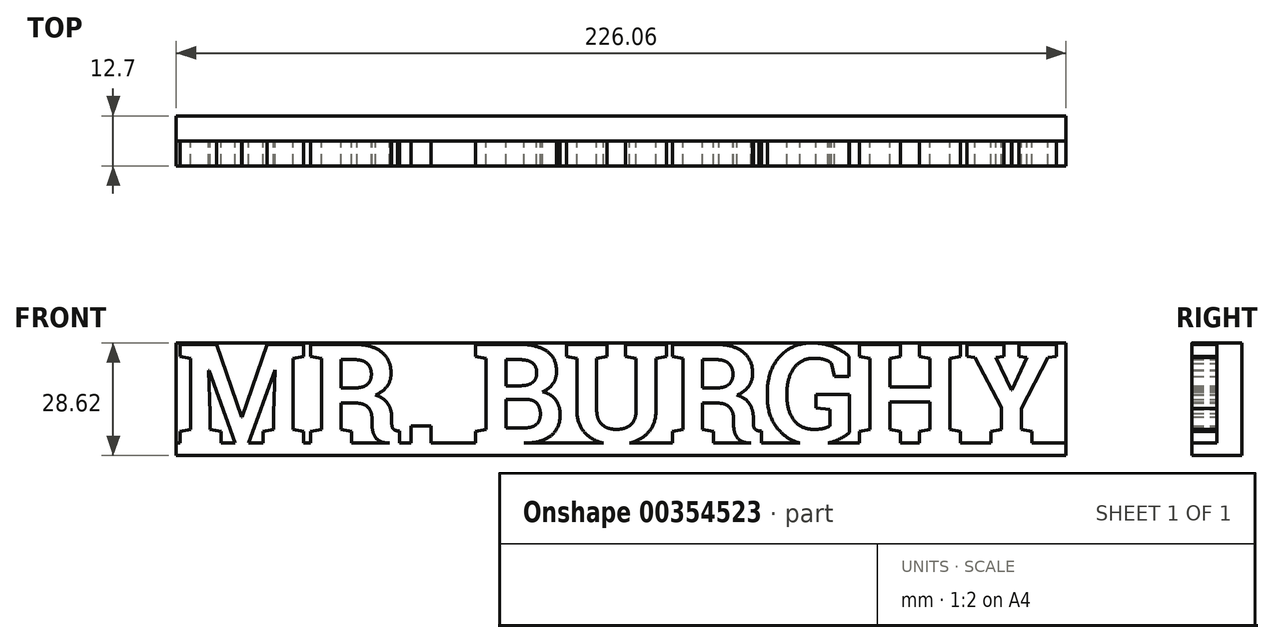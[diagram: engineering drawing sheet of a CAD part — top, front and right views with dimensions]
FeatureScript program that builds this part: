
annotation { "Feature Type Name" : "Feature", "Feature Type Description" : "" }
export const myFeature = defineFeature(function(context is Context, id is Id, definition is map)
    precondition{}
    {
        {
            var Q0;
            Q0=qCreatedBy(makeId("Front.planeOp"),FACE);
            var sketch = newSketch(context, id + "F0", { "sketchPlane" : qUnion([Q0])});
            skLineSegment(sketch, "E0.bottom", {"start": v(113.03, 0) * mm, "end": v(-113.03, 0) * mm});
            skLineSegment(sketch, "E0.top", {"start": v(113.03, 25.4) * mm, "end": v(-113.03, 25.4) * mm});
            skLineSegment(sketch, "E0.left", {"start": v(113.03, 0) * mm, "end": v(113.03, 25.4) * mm});
            skLineSegment(sketch, "E0.right", {"start": v(-113.03, 0) * mm, "end": v(-113.03, 25.4) * mm});
            skPoint(sketch, "E0.middle", {"position": v(0, 12.7) * mm});
            skSolve(sketch);
        }
        {
            var Q0;
            Q0 = qSketchRegion(id + "F0", true);
            extrude(context, id + "F1", {"entities" : qUnion([Q0]), "depth" : 6.35 * mm});
        }
        {
            var Q0;
            Q0=makeQuery(id+"F1.opExtrude","CAP_FACE",FACE,{"disambiguationData":[OSD([sQuery(id+"F0.wireOp",EDGE,"E0.bottom"),sQuery(id+"F0.wireOp",EDGE,"E0.top"),sQuery(id+"F0.wireOp",EDGE,"E0.left"),sQuery(id+"F0.wireOp",EDGE,"E0.right")])],"isStart":false});
            var sketch = newSketch(context, id + "F2", { "sketchPlane" : qUnion([Q0])});
            skText(sketch, "E1", { "text": "MR. BURGHY", "fontName": "RobotoSlab-Bold.ttf"});
            const initialGuessF2  = {"E1": [-0.11303, 0, 1, 0, 0.0254]};
            skSetInitialGuess(sketch, initialGuessF2);
            skSolve(sketch);
        }
        {
            var Q0;
            Q0 = qSketchRegion(id + "F2", true);
            extrude(context, id + "F3", {"entities" : qUnion([Q0]), "operationType" : NewBodyOperationType.ADD, "depth" : 6.35 * mm});
        }
        {
            var Q0;
            Q0=qCreatedBy(makeId("Top.planeOp"),FACE);
            var sketch = newSketch(context, id + "F4", { "sketchPlane" : qUnion([Q0])});
            skLineSegment(sketch, "E2.bottom", {"start": v(-113.03, 0) * mm, "end": v(113.03, 0) * mm});
            skLineSegment(sketch, "E2.top", {"start": v(-113.03, -12.7) * mm, "end": v(113.03, -12.7) * mm});
            skLineSegment(sketch, "E2.left", {"start": v(-113.03, 0) * mm, "end": v(-113.03, -12.7) * mm});
            skLineSegment(sketch, "E2.right", {"start": v(113.03, 0) * mm, "end": v(113.03, -12.7) * mm});
            skSolve(sketch);
        }
        {
            var Q0;
            Q0 = qSketchRegion(id + "F4", true);
            extrude(context, id + "F5", {"entities" : qUnion([Q0]), "operationType" : NewBodyOperationType.ADD, "oppositeDirection" : true, "depth" : 3.17 * mm});
        }
    });
